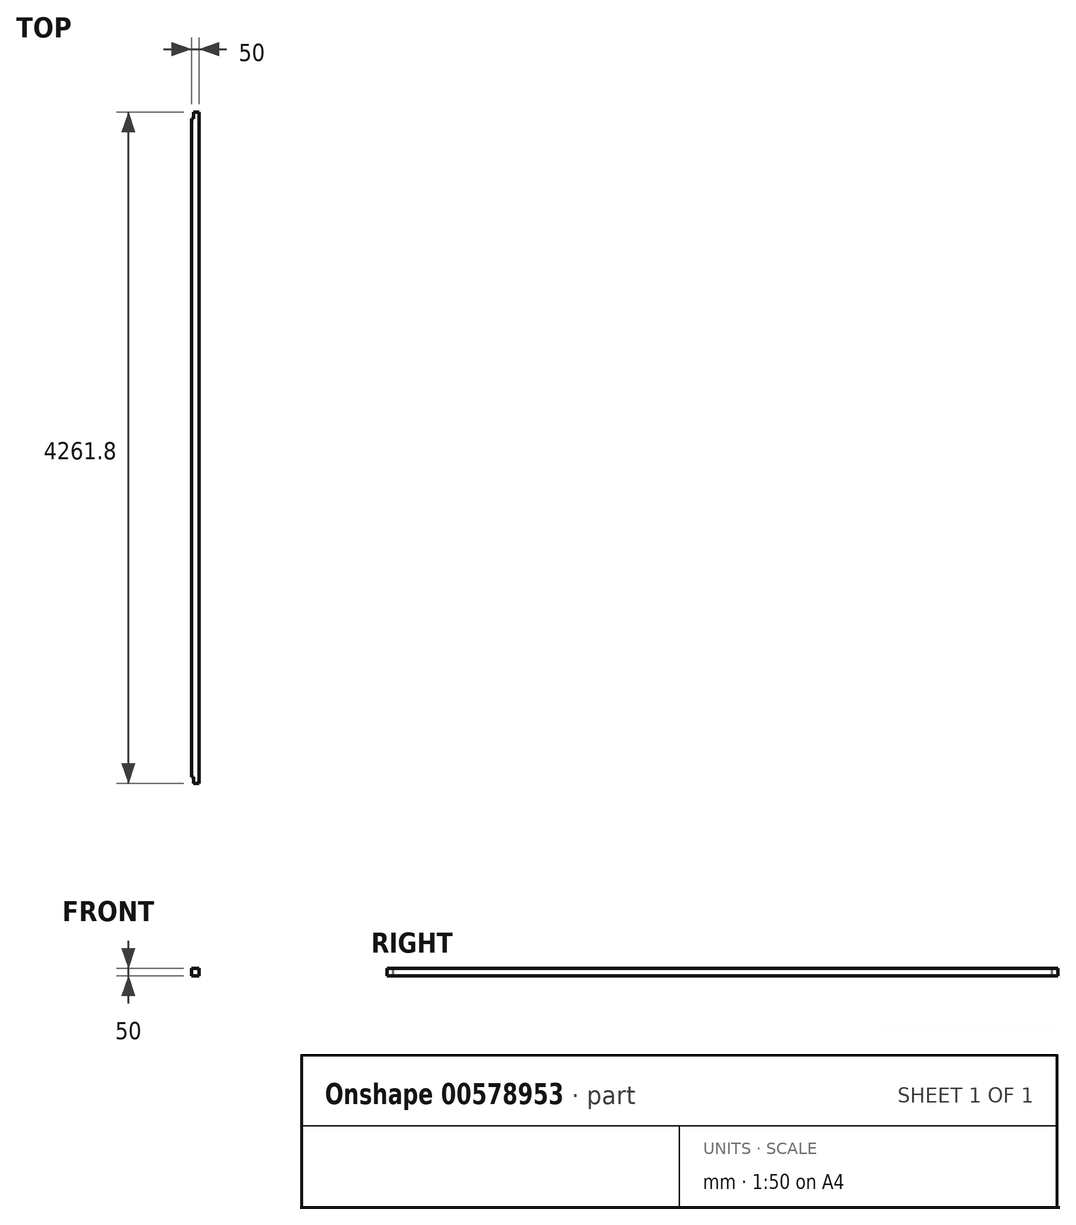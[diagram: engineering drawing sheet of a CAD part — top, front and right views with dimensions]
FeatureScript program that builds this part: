
annotation { "Feature Type Name" : "Feature", "Feature Type Description" : "" }
export const myFeature = defineFeature(function(context is Context, id is Id, definition is map)
    precondition{}
    {
        {
            var Q0;
            Q0=qCreatedBy(makeId("Front.planeOp"),FACE);
            var sketch = newSketch(context, id + "F0", { "sketchPlane" : qUnion([Q0])});
            skLineSegment(sketch, "E0.bottom", {"start": v(25, 25) * mm, "end": v(-25, 25) * mm});
            skLineSegment(sketch, "E0.top", {"start": v(25, -25) * mm, "end": v(-25, -25) * mm});
            skLineSegment(sketch, "E0.left", {"start": v(25, 25) * mm, "end": v(25, -25) * mm});
            skLineSegment(sketch, "E0.right", {"start": v(-25, 25) * mm, "end": v(-25, -25) * mm});
            skPoint(sketch, "E0.middle", {"position": v(0, 0) * mm});
            skLineSegment(sketch, "E1.bottom", {"start": v(24, 24) * mm, "end": v(-24, 24) * mm});
            skLineSegment(sketch, "E1.top", {"start": v(24, -24) * mm, "end": v(-24, -24) * mm});
            skLineSegment(sketch, "E1.left", {"start": v(24, 24) * mm, "end": v(24, -24) * mm});
            skLineSegment(sketch, "E1.right", {"start": v(-24, 24) * mm, "end": v(-24, -24) * mm});
            skSolve(sketch);
        }
        {
            var Q0;
            Q0=makeQuery(id+"F0.imprint","IMPRINT",FACE,{"disambiguationData":[TD([[makeQuery(id+"F0.imprint","IMPRINT",EDGE,{"derivedFrom":sQuery(id+"F0.wireOp",EDGE,"E0.bottom")}),1.0]])]});
            extrude(context, id + "F1", {"entities" : qUnion([Q0]), "endBound" : BoundingType.SYMMETRIC, "depth" : (((4201.3 + 60) + 0.5)) * mm, "offsetDistance" : 25 * mm});
        }
        {
            var Q0;
            Q0=makeQuery(id+"F1.opExtrude","SWEPT_FACE",FACE,{"disambiguationData":[OSD([sQuery(id+"F0.wireOp",EDGE,"E0.right")])]});
            var sketch = newSketch(context, id + "F2", { "sketchPlane" : qUnion([Q0])});
            skLineSegment(sketch, "E2.top", {"start": v(2130.9, -25) * mm, "end": v(2091.9, -25) * mm});
            skLineSegment(sketch, "E2.left", {"start": v(2130.9, 25) * mm, "end": v(2130.9, -25) * mm});
            skLineSegment(sketch, "E2.right", {"start": v(2091.9, 25) * mm, "end": v(2091.9, -25) * mm});
            skLineSegment(sketch, "E3.bottom", {"start": v(-2130.9, 25) * mm, "end": v(-2091.9, 25) * mm});
            skLineSegment(sketch, "E3.top", {"start": v(-2130.9, -25) * mm, "end": v(-2091.9, -25) * mm});
            skLineSegment(sketch, "E3.left", {"start": v(-2130.9, 25) * mm, "end": v(-2130.9, -25) * mm});
            skLineSegment(sketch, "E3.right", {"start": v(-2091.9, 25) * mm, "end": v(-2091.9, -25) * mm});
            skSolve(sketch);
        }
        {
            var Q0;
            Q0=makeQuery(id+"F2.imprint","IMPRINT",FACE,{"disambiguationData":[TD([[makeQuery(id+"F2.imprint","IMPRINT",EDGE,{"derivedFrom":sQuery(id+"F2.wireOp",EDGE,"E3.bottom")}),1.0]])]});
            var Q1;
            Q1=makeQuery(id+"F2.imprint","IMPRINT",FACE,{"disambiguationData":[TD([[makeQuery(id+"F2.imprint","IMPRINT",EDGE,{"derivedFrom":sQuery(id+"F2.wireOp",EDGE,"E2.top")}),-1.0]])]});
            extrude(context, id + "F3", {"entities" : qUnion([Q0, Q1]), "operationType" : NewBodyOperationType.REMOVE, "oppositeDirection" : true, "depth" : 15 * mm, "offsetDistance" : 25 * mm});
        }
    });
